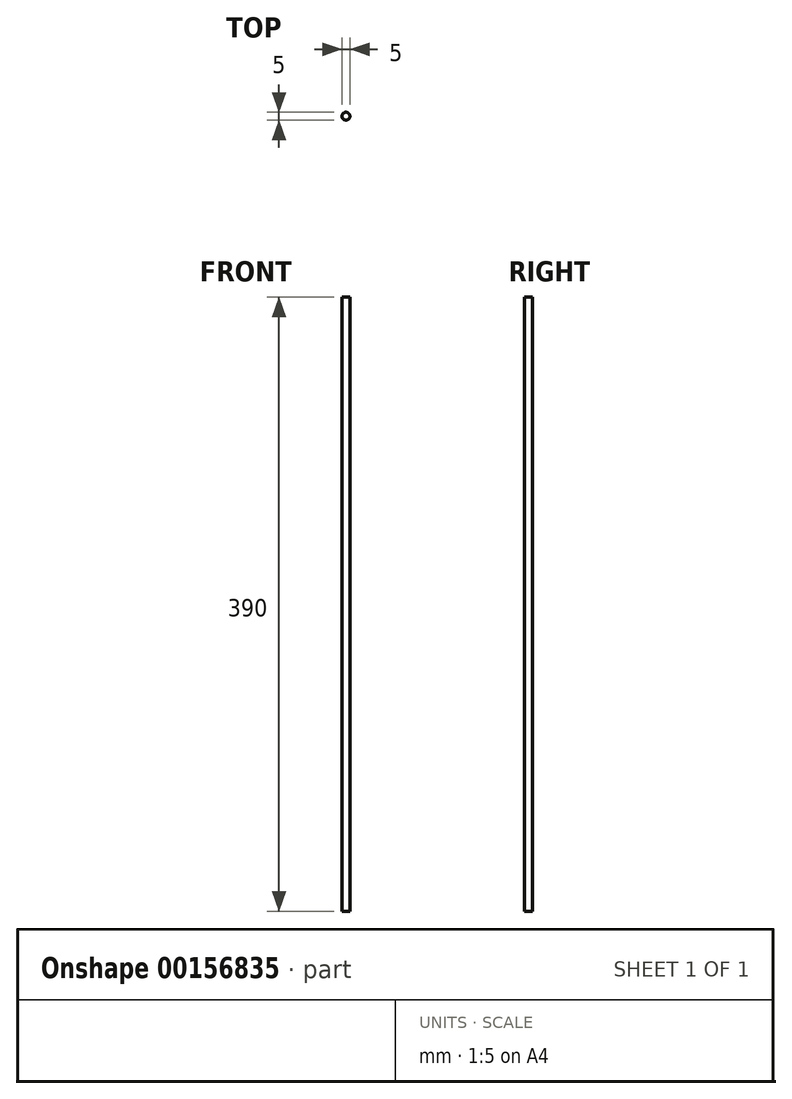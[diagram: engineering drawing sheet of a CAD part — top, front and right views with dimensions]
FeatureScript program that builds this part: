
annotation { "Feature Type Name" : "Feature", "Feature Type Description" : "" }
export const myFeature = defineFeature(function(context is Context, id is Id, definition is map)
    precondition{}
    {
        {
            var Q0;
            Q0=qCreatedBy(makeId("Top.planeOp"),FACE);
            var sketch = newSketch(context, id + "F0", { "sketchPlane" : qUnion([Q0])});
            skCircle(sketch, "E0", {"center": v(0, 0) * mm, "radius": 2.5 * mm});
            skSolve(sketch);
        }
        {
            var Q0;
            Q0=qSketchRegion(id+"F0",true);
            extrude(context, id + "F1", {"entities" : qUnion([Q0]), "endBound" : BoundingType.SYMMETRIC, "depth" : 390 * mm});
        }
    });
